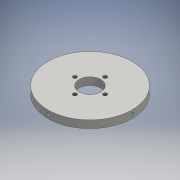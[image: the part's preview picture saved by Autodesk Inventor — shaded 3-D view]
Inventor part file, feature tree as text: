
AUTODESK INVENTOR PART (.ipt)
format: ipt  version: 2016 (Build 200138000, 138)  size: 148,480 bytes
history: native  units: mm
features: thread x8, extrude x6, sketch x6, other x5
ambient origin geometry x8: Origin, YZ Plane, XZ Plane, XY Plane, X Axis, Y Axis, Z Axis, Center Point
bodies: Body1 (feature_tree)
feature tree (25):
  other  "ソリッド1"
  extrude  "押し出し1"  Depth=89.0mm
  extrude  "押し出し2"  Depth=23.0mm
  other  "作業平面1"
  extrude  "押し出し3"  Depth=8.0mm TaperAngle=0.0deg
  other  "作業平面2"
  extrude  "押し出し4"  Depth=16.0mm
  other  "作業平面3"
  extrude  "押し出し5"  Depth=4.0mm
  other  "作業平面4"
  extrude  "押し出し6"  Depth=40.0mm TaperAngle=360.0deg
  thread  "ねじ2"
  thread  "ねじ3"
  thread  "ねじ4"
  thread  "ねじ5"
  thread  "ねじ6"
  thread  "ねじ7"
  thread  "ねじ8"
  thread  "ねじ9"
  sketch  "スケッチ1"
  sketch  "スケッチ2"
  sketch  "スケッチ3"
  sketch  "スケッチ4"
  sketch  "スケッチ5"
  sketch  "スケッチ6"
